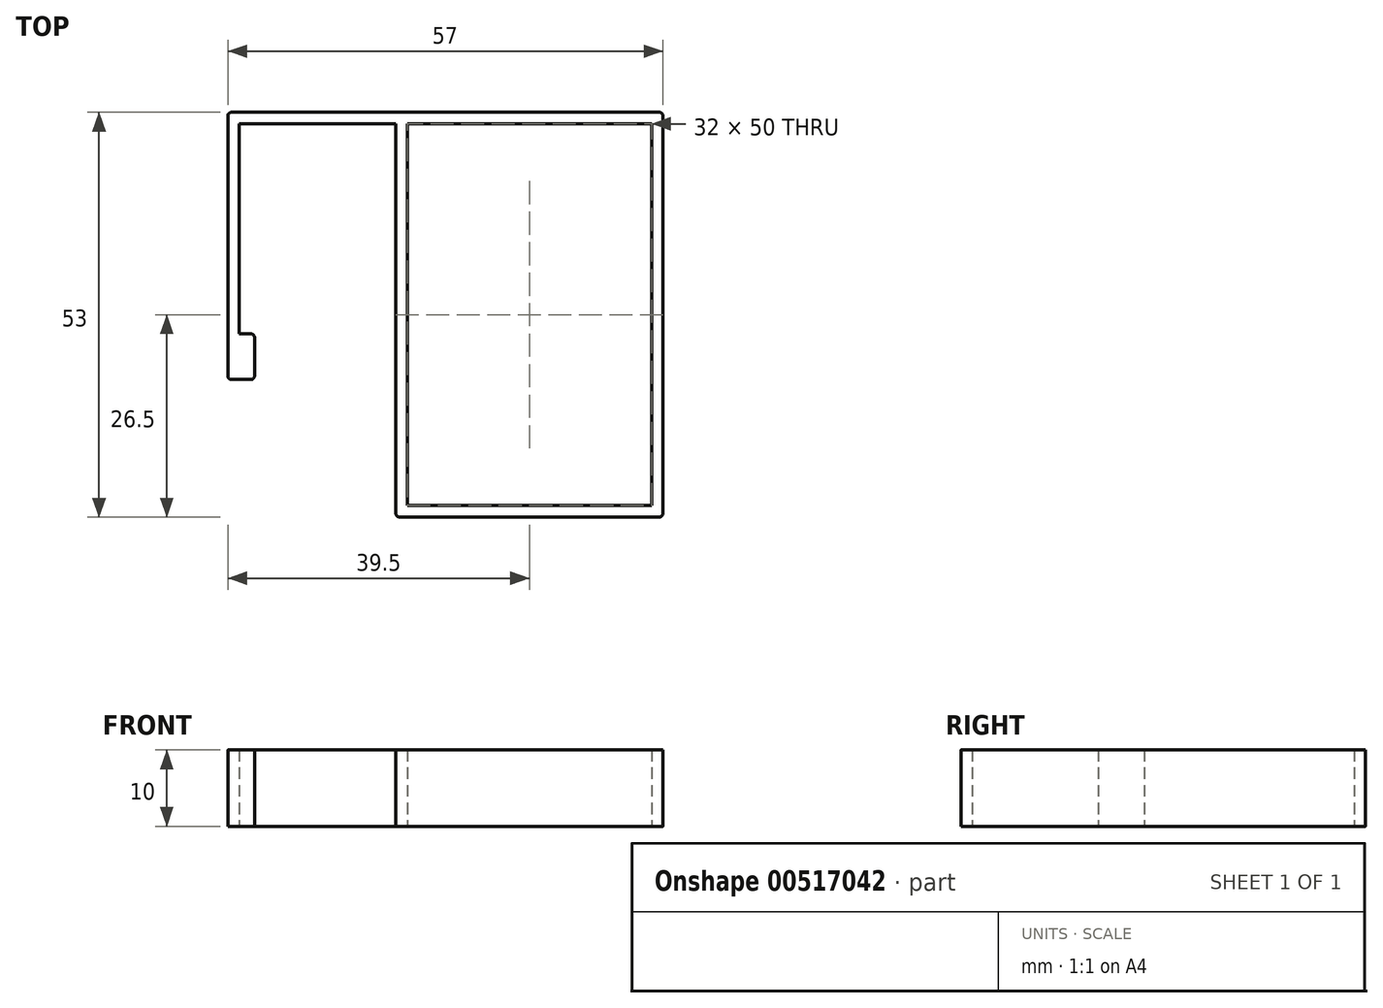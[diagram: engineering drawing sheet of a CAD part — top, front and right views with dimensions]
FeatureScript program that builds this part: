
annotation { "Feature Type Name" : "Feature", "Feature Type Description" : "" }
export const myFeature = defineFeature(function(context is Context, id is Id, definition is map)
    precondition{}
    {
        {
            var Q0;
            Q0=qCreatedBy(makeId("Top.planeOp"),FACE);
            var sketch = newSketch(context, id + "F0", { "sketchPlane" : qUnion([Q0])});
            skLineSegment(sketch, "E0.bottom", {"start": v(16, 25) * mm, "end": v(-16, 25) * mm});
            skLineSegment(sketch, "E0.top", {"start": v(16, -25) * mm, "end": v(-16, -25) * mm});
            skLineSegment(sketch, "E0.left", {"start": v(16, 25) * mm, "end": v(16, -25) * mm});
            skLineSegment(sketch, "E0.right", {"start": v(-16, 25) * mm, "end": v(-16, -25) * mm});
            skPoint(sketch, "E0.middle", {"position": v(0, 0) * mm});
            skLineSegment(sketch, "E1", {"start": v(-16, 25) * mm, "end": v(-38, 25) * mm});
            skLineSegment(sketch, "E2", {"start": v(-38, 25) * mm, "end": v(-38, -8.5) * mm});
            skLineSegment(sketch, "E3.0", {"start": v(-17.5, 26.5) * mm, "end": v(-17.5, -26.5) * mm});
            skLineSegment(sketch, "E3.1", {"start": v(17.5, 26.5) * mm, "end": v(-17.5, 26.5) * mm});
            skLineSegment(sketch, "E3.2", {"start": v(17.5, 26.5) * mm, "end": v(17.5, -26.5) * mm});
            skLineSegment(sketch, "E3.3", {"start": v(17.5, -26.5) * mm, "end": v(-17.5, -26.5) * mm});
            skLineSegment(sketch, "E4.0", {"start": v(-39.5, 26.5) * mm, "end": v(-39.5, -8.5) * mm});
            skLineSegment(sketch, "E4.1", {"start": v(-16, 26.5) * mm, "end": v(-39.5, 26.5) * mm});
            skLineSegment(sketch, "E5", {"start": v(-39.5, -8.5) * mm, "end": v(-38, -8.5) * mm});
            skLineSegment(sketch, "E6", {"start": v(-38, -8.5) * mm, "end": v(-36, -8.5) * mm});
            skLineSegment(sketch, "E7", {"start": v(-36, -8.5) * mm, "end": v(-36, -2.5) * mm});
            skLineSegment(sketch, "E8", {"start": v(-36, -2.5) * mm, "end": v(-38, -2.5) * mm});
            skSolve(sketch);
        }
        {
            var Q0;
            Q0 = qSketchRegion(id + "F0", true);
            extrude(context, id + "F1", {"entities" : qUnion([Q0]), "depth" : 10 * mm, "offsetDistance" : 25 * mm});
        }
        {
            var Q0;
            Q0=makeQuery(id+"F1.opExtrude","SWEPT_EDGE",EDGE,{"disambiguationData":[OSD([sQuery(id+"F0.wireOp",EDGE,"E7"),sQuery(id+"F0.wireOp",EDGE,"E8")])]});
            var Q1;
            Q1=makeQuery(id+"F1.opExtrude","SWEPT_EDGE",EDGE,{"disambiguationData":[OSD([sQuery(id+"F0.wireOp",EDGE,"E6"),sQuery(id+"F0.wireOp",EDGE,"E7")])]});
            var Q2;
            Q2=makeQuery(id+"F1.opExtrude","SWEPT_EDGE",EDGE,{"disambiguationData":[OSD([sQuery(id+"F0.wireOp",EDGE,"E3.2"),sQuery(id+"F0.wireOp",EDGE,"E3.3")])]});
            var Q3;
            Q3=makeQuery(id+"F1.opExtrude","SWEPT_EDGE",EDGE,{"disambiguationData":[OSD([sQuery(id+"F0.wireOp",EDGE,"E3.1"),sQuery(id+"F0.wireOp",EDGE,"E3.2")])]});
            var Q4;
            Q4=makeQuery(id+"F1.opExtrude","SWEPT_EDGE",EDGE,{"disambiguationData":[OSD([sQuery(id+"F0.wireOp",EDGE,"E3.0"),sQuery(id+"F0.wireOp",EDGE,"E3.3")])]});
            var Q5;
            Q5=makeQuery(id+"F1.opExtrude","SWEPT_EDGE",EDGE,{"disambiguationData":[OSD([sQuery(id+"F0.wireOp",EDGE,"E4.0"),sQuery(id+"F0.wireOp",EDGE,"E4.1")])]});
            var Q6;
            Q6=makeQuery(id+"F1.opExtrude","SWEPT_EDGE",EDGE,{"disambiguationData":[OSD([sQuery(id+"F0.wireOp",EDGE,"E4.0"),sQuery(id+"F0.wireOp",EDGE,"E5")])]});
            fillet(context, id + "F2", {"entities" : qUnion([Q0, Q1, Q2, Q3, Q4, Q5, Q6]), "radius" : .5 * mm, "tangentPropagation" : true, "allowEdgeOverflow" : false});
        }
    });
